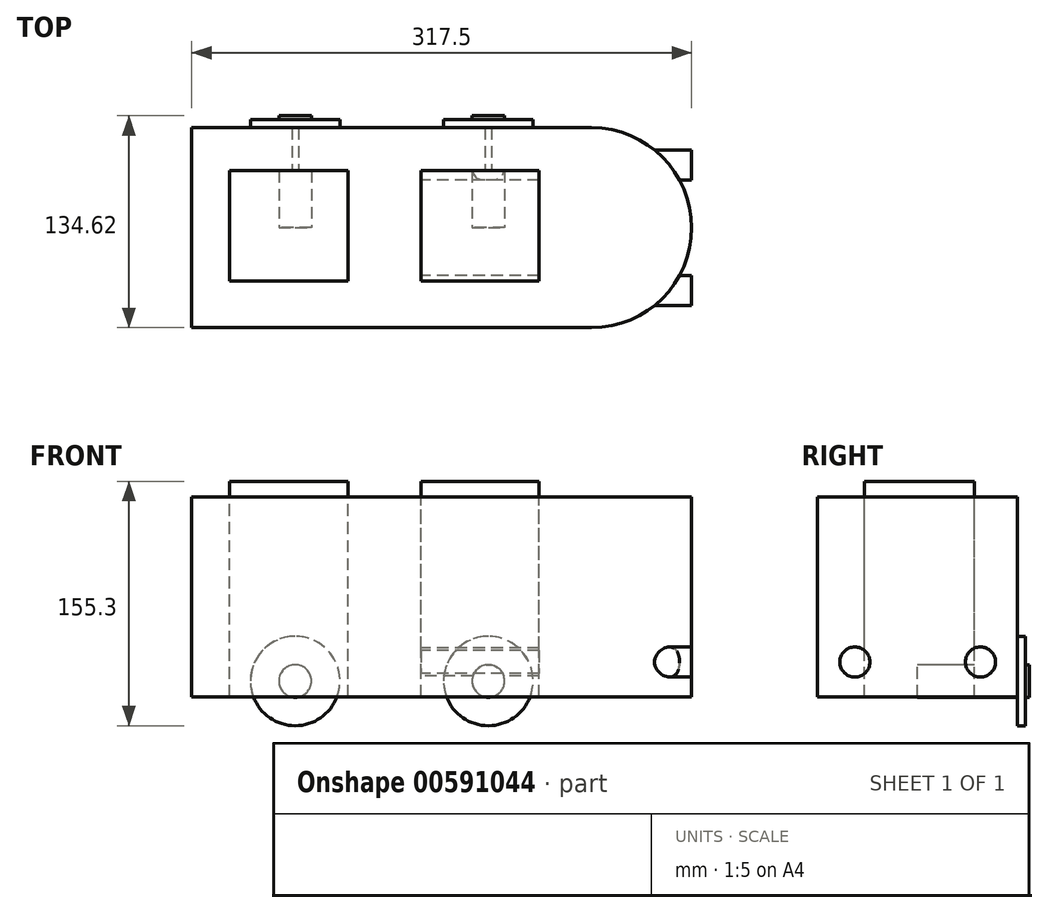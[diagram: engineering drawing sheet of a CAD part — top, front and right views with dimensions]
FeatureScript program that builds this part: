
annotation { "Feature Type Name" : "Feature", "Feature Type Description" : "" }
export const myFeature = defineFeature(function(context is Context, id is Id, definition is map)
    precondition{}
    {
        {
            var Q0;
            Q0=qCreatedBy(makeId("Top.planeOp"),FACE);
            var sketch = newSketch(context, id + "F0", { "sketchPlane" : qUnion([Q0])});
            skLineSegment(sketch, "E0.bottom", {"start": v(127, -63.5) * mm, "end": v(-127, -63.5) * mm});
            skLineSegment(sketch, "E0.top", {"start": v(127, 63.5) * mm, "end": v(-127, 63.5) * mm});
            skLineSegment(sketch, "E0.right", {"start": v(-127, -63.5) * mm, "end": v(-127, 63.5) * mm});
            skPoint(sketch, "E0.middle", {"position": v(0, 0) * mm});
            skLineSegment(sketch, "E1.bottom", {"start": v(18.65, 36.22) * mm, "end": v(93.65, 36.22) * mm});
            skLineSegment(sketch, "E1.top", {"start": v(18.65, -33.78) * mm, "end": v(93.65, -33.78) * mm});
            skLineSegment(sketch, "E1.left", {"start": v(18.65, 36.22) * mm, "end": v(18.65, -33.78) * mm});
            skLineSegment(sketch, "E1.right", {"start": v(93.65, 36.22) * mm, "end": v(93.65, -33.78) * mm});
            skLineSegment(sketch, "E2.bottom", {"start": v(-27.88, 36.22) * mm, "end": v(-102.88, 36.22) * mm});
            skLineSegment(sketch, "E2.top", {"start": v(-27.88, -33.78) * mm, "end": v(-102.88, -33.78) * mm});
            skLineSegment(sketch, "E2.left", {"start": v(-27.88, 36.22) * mm, "end": v(-27.88, -33.78) * mm});
            skLineSegment(sketch, "E2.right", {"start": v(-102.88, 36.22) * mm, "end": v(-102.88, -33.78) * mm});
            skArc(sketch, "E3", {"start": v(-125.5, 63.5) * mm, "mid": v(-189.75, 0) * mm, "end": v(-125.5, -63.5) * mm});
            skPoint(sketch, "E3.third.point", {"position": v(-189.75, 0) * mm});
            skArc(sketch, "E4", {"start": v(127, -63.5) * mm, "mid": v(190.5, 0) * mm, "end": v(127, 63.5) * mm});
            skPoint(sketch, "E4.third.point", {"position": v(190.5, 0) * mm});
            skPoint(sketch, "E4.third.point.positionSnap0", {"position": v(127, 0) * mm});
            skLineSegment(sketch, "E5", {"start": v(-127, 63.5) * mm, "end": v(-127, -63.5) * mm});
            skLineSegment(sketch, "E6", {"start": v(127, 63.5) * mm, "end": v(127, -63.5) * mm});
            skSolve(sketch);
        }
        {
            var Q0;
            Q0=makeQuery(id+"F0.imprint","IMPRINT",FACE,{"disambiguationData":[TD([[makeQuery(id+"F0.imprint","IMPRINT",EDGE,{"derivedFrom":sQuery(id+"F0.wireOp",EDGE,"E1.bottom")}),-1.0]])]});
            extrude(context, id + "F1", {"entities" : qUnion([Q0]), "depth" : 10 * mm, "offsetDistance" : 25.4 * mm});
        }
        {
            var Q0;
            Q0=makeQuery(id+"F0.imprint","IMPRINT",FACE,{"disambiguationData":[TD([[makeQuery(id+"F0.imprint","IMPRINT",EDGE,{"derivedFrom":sQuery(id+"F0.wireOp",EDGE,"E2.bottom")}),1.0]])]});
            extrude(context, id + "F2", {"entities" : qUnion([Q0]), "operationType" : NewBodyOperationType.ADD, "depth" : 10 * mm, "offsetDistance" : 25.4 * mm});
        }
        {
            var Q0;
            {var subQ0=sQuery(id+"F0.wireOp",EDGE,"E5");Q0=makeQuery(id+"F0.imprint","IMPRINT",FACE,{"disambiguationData":[TD([[makeQuery(id+"F0.imprint","IMPRINT",EDGE,{"derivedFrom":subQ0}),-1.0]])]});}
            var Q1;
            Q1=makeQuery(id+"F0.imprint","IMPRINT",FACE,{"disambiguationData":[TD([[makeQuery(id+"F0.imprint","IMPRINT",EDGE,{"derivedFrom":sQuery(id+"F0.wireOp",EDGE,"E1.bottom")}),1.0]])]});
            var Q2;
            Q2=makeQuery(id+"F0.imprint","IMPRINT",FACE,{"disambiguationData":[TD([[makeQuery(id+"F0.imprint","IMPRINT",EDGE,{"derivedFrom":sQuery(id+"F0.wireOp",EDGE,"E4")}),1.0]])]});
            extrude(context, id + "F3", {"entities" : qUnion([Q0, Q1, Q2]), "oppositeDirection" : true, "depth" : 127 * mm, "offsetDistance" : 25.4 * mm});
        }
        {
            var Q0;
            Q0=qCreatedBy(makeId("Right.planeOp"),FACE);
            var sketch = newSketch(context, id + "F4", { "sketchPlane" : qUnion([Q0])});
            skCircle(sketch, "E7", {"center": v(39.9, -104.85) * mm, "radius": 9.56 * mm});
            skCircle(sketch, "E8.MirrorC", {"center": v(-39.9, -104.85) * mm, "radius": 9.56 * mm});
            skSolve(sketch);
        }
        {
            var Q0;
            Q0 = qSketchRegion(id + "F4", true);
            var Q1;
            Q1=sQuery(id+"F4.wireOp",EDGE,"E7");
            var Q2;
            Q2=sQuery(id+"F4.wireOp",EDGE,"E8.MirrorC");
            extrude(context, id + "F5", {"entities" : qUnion([Q0]), "operationType" : NewBodyOperationType.ADD, "surfaceEntities" : qUnion([Q1, Q2]), "depth" : 190.5 * mm, "offsetDistance" : 25.4 * mm});
        }
        {
            var Q0;
            Q0=qCreatedBy(makeId("Front.planeOp"),FACE);
            var sketch = newSketch(context, id + "F6", { "sketchPlane" : qUnion([Q0])});
            skCircle(sketch, "E9", {"center": v(61.33, -116.9) * mm, "radius": 10.32 * mm});
            skCircle(sketch, "E10.MirrorC", {"center": v(-61.33, -116.9) * mm, "radius": 10.32 * mm});
            skSolve(sketch);
        }
        {
            var Q0;
            Q0 = qSketchRegion(id + "F6", true);
            extrude(context, id + "F7", {"entities" : qUnion([Q0]), "operationType" : NewBodyOperationType.ADD, "oppositeDirection" : true, "depth" : 71.12 * mm, "offsetDistance" : 25.4 * mm});
        }
        {
            var Q0;
            Q0=makeQuery(id+"F3.opExtrude","SWEPT_FACE",FACE,{"disambiguationData":[OSD([sQuery(id+"F0.wireOp",EDGE,"E0.top")])]});
            var sketch = newSketch(context, id + "F8", { "sketchPlane" : qUnion([Q0])});
            skCircle(sketch, "E11", {"center": v(-61.33, -116.9) * mm, "radius": 28.4 * mm});
            skCircle(sketch, "E12.MirrorC", {"center": v(61.33, -116.9) * mm, "radius": 28.4 * mm});
            skSolve(sketch);
        }
        {
            var Q0;
            Q0 = qSketchRegion(id + "F8", true);
            extrude(context, id + "F9", {"entities" : qUnion([Q0]), "operationType" : NewBodyOperationType.ADD, "depth" : 5.08 * mm, "offsetDistance" : 25.4 * mm});
        }
    });
